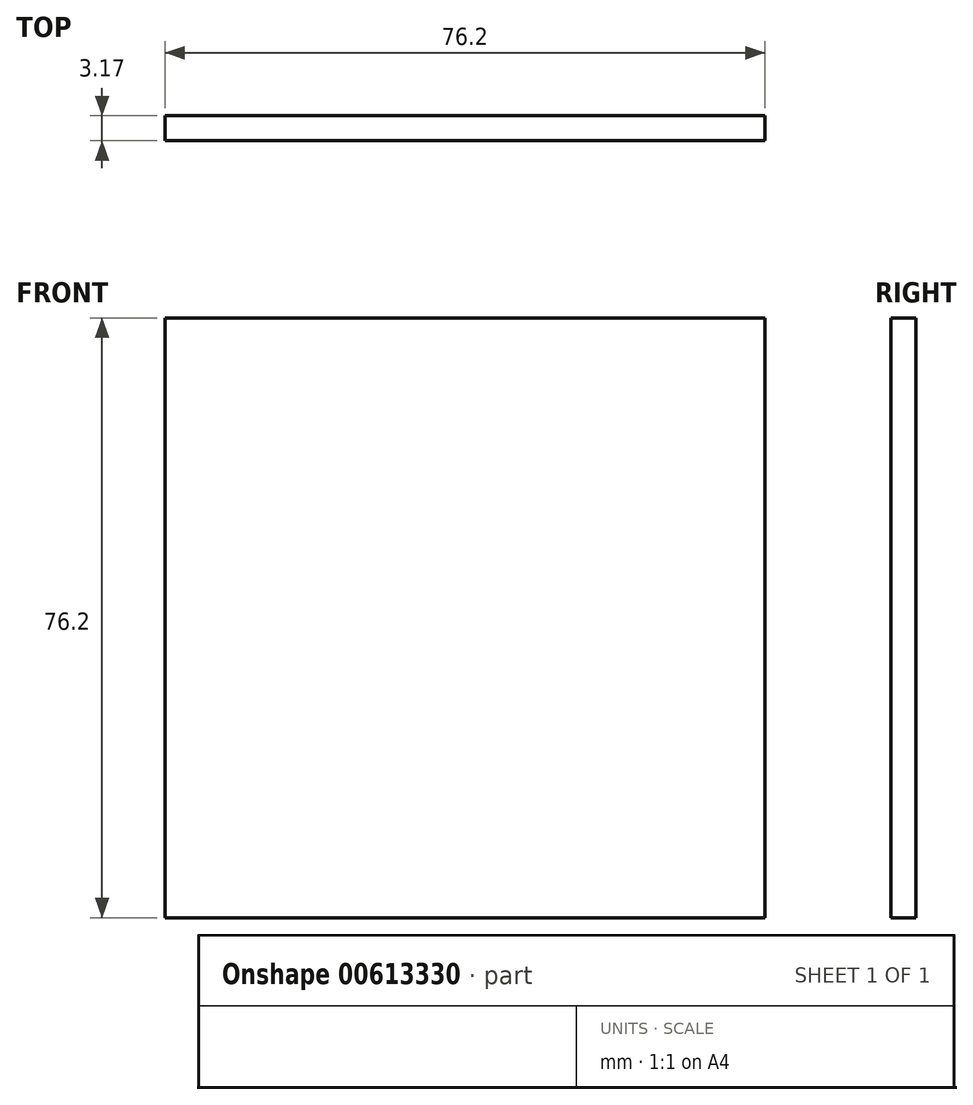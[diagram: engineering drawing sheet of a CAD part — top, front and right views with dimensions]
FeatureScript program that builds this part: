
annotation { "Feature Type Name" : "Feature", "Feature Type Description" : "" }
export const myFeature = defineFeature(function(context is Context, id is Id, definition is map)
    precondition{}
    {
        {
            var Q0;
            Q0=qCreatedBy(makeId("Front.planeOp"),FACE);
            var sketch = newSketch(context, id + "F0", { "sketchPlane" : qUnion([Q0])});
            skLineSegment(sketch, "E0.bottom", {"start": v(38.1, 38.1) * mm, "end": v(-38.1, 38.1) * mm});
            skLineSegment(sketch, "E0.top", {"start": v(38.1, -38.1) * mm, "end": v(-38.1, -38.1) * mm});
            skLineSegment(sketch, "E0.left", {"start": v(38.1, 38.1) * mm, "end": v(38.1, -38.1) * mm});
            skLineSegment(sketch, "E0.right", {"start": v(-38.1, 38.1) * mm, "end": v(-38.1, -38.1) * mm});
            skPoint(sketch, "E0.middle", {"position": v(0, 0) * mm});
            skSolve(sketch);
        }
        {
            var Q0;
            Q0 = qSketchRegion(id + "F0", true);
            extrude(context, id + "F1", {"entities" : qUnion([Q0]), "depth" : 3.17 * mm, "offsetDistance" : 25.4 * mm});
        }
    });
